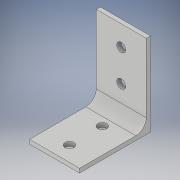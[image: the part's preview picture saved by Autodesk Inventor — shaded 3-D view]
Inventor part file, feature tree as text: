
AUTODESK INVENTOR PART (.ipt)
format: ipt  version: 2019 (Build 230136000, 136)  size: 144,384 bytes
history: native  units: in
note: dims shown in document units (in); Inventor stores cm internally (conversion verified against a paired STEP export)
features: extrude x4, sketch x4, fillet x1
ambient origin geometry x8: Origin, YZ Plane, XZ Plane, XY Plane, X Axis, Y Axis, Z Axis, Center Point
bodies: Solid1 (feature_tree)
feature tree (9):
  extrude  "Extrusion1"  Depth=0.6in
  extrude  "Extrusion2"  Depth=0.05in
  extrude  "Extrusion3"  Depth=0.8in
  fillet  "Fillet1"  Radius=0.107in
  sketch  "Sketch1"  dims[d0=1.0in d1=0.6in]
  sketch  "Sketch2"  dims[d2=0.05in d3=0.0in d4=0.05in]
  sketch  "Sketch3"  dims[d5=0.8in d6=0.0in d7=0.107in d8=0.107in]
  sketch  "Sketch4"  dims[d10=0.3in d11=0.379in d13=1.0in d14=0.0in d15=0.107in d17=0.394in d19=0.107in d22=0.0in d23=1.0in d24=0.125in d25=0.377in d26=0.3in d27=0.3in d28=0.3in]
  extrude  "Extrusion4"  Depth=0.125in
